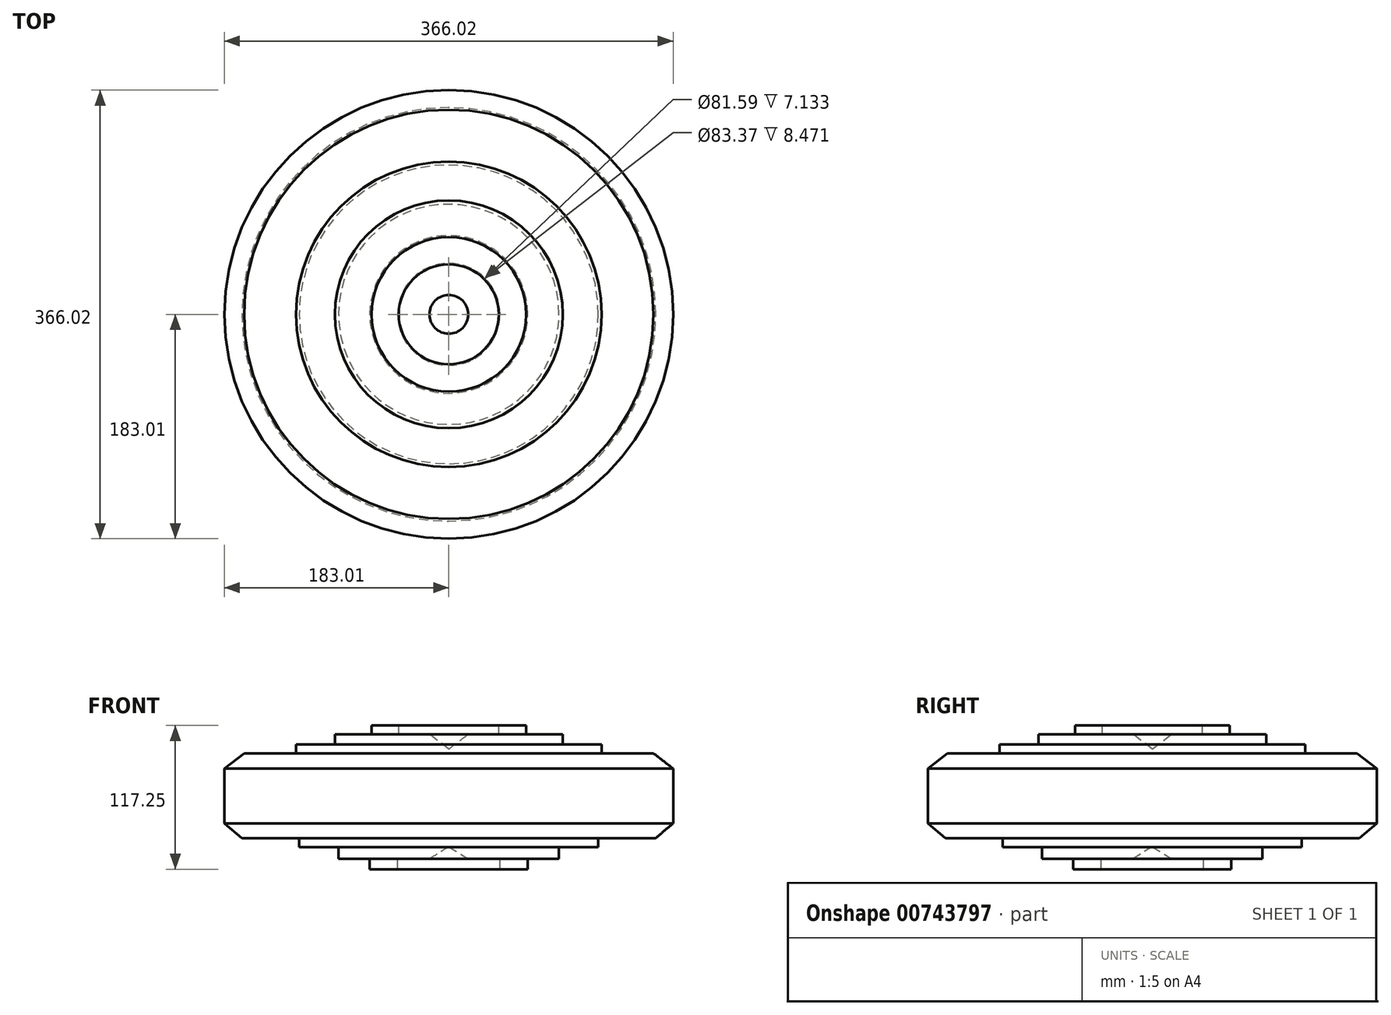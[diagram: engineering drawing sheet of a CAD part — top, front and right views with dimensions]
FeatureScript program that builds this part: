
annotation { "Feature Type Name" : "Feature", "Feature Type Description" : "" }
export const myFeature = defineFeature(function(context is Context, id is Id, definition is map)
    precondition{}
    {
        {
            var Q0;
            Q0=qCreatedBy(makeId("Front.planeOp"),FACE);
            var sketch = newSketch(context, id + "F0", { "sketchPlane" : qUnion([Q0])});
            skLineSegment(sketch, "E0", {"start": v(0, 39.9) * mm, "end": v(0, -39.9) * mm});
            skLineSegment(sketch, "E1", {"start": v(0, 39.9) * mm, "end": v(15.83, 51.94) * mm});
            skLineSegment(sketch, "E2", {"start": v(0, -39.9) * mm, "end": v(15.83, -49.7) * mm});
            skLineSegment(sketch, "E3", {"start": v(15.83, 51.94) * mm, "end": v(40.8, 51.94) * mm});
            skLineSegment(sketch, "E4", {"start": v(40.8, 51.94) * mm, "end": v(40.8, 59.07) * mm});
            skLineSegment(sketch, "E5", {"start": v(40.8, 59.07) * mm, "end": v(63.08, 59.07) * mm});
            skLineSegment(sketch, "E6", {"start": v(63.08, 59.07) * mm, "end": v(63.08, 51.94) * mm});
            skLineSegment(sketch, "E7", {"start": v(63.08, 51.94) * mm, "end": v(92.95, 51.94) * mm});
            skLineSegment(sketch, "E8", {"start": v(92.95, 51.94) * mm, "end": v(92.95, 43.47) * mm});
            skLineSegment(sketch, "E9", {"start": v(92.95, 43.47) * mm, "end": v(124.6, 43.47) * mm});
            skLineSegment(sketch, "E10", {"start": v(124.6, 43.47) * mm, "end": v(124.6, 36.33) * mm});
            skLineSegment(sketch, "E11", {"start": v(124.6, 36.33) * mm, "end": v(166.96, 36.33) * mm});
            skLineSegment(sketch, "E12", {"start": v(15.83, -49.7) * mm, "end": v(41.68, -49.7) * mm});
            skLineSegment(sketch, "E13", {"start": v(41.68, -49.7) * mm, "end": v(41.68, -58.18) * mm});
            skLineSegment(sketch, "E14", {"start": v(41.68, -58.18) * mm, "end": v(64.87, -58.18) * mm});
            skLineSegment(sketch, "E15", {"start": v(64.42, -58.63) * mm, "end": v(64.42, -49.7) * mm});
            skLineSegment(sketch, "E16", {"start": v(64.42, -49.7) * mm, "end": v(89.83, -49.7) * mm});
            skLineSegment(sketch, "E17", {"start": v(89.83, -49.7) * mm, "end": v(89.83, -40.35) * mm});
            skLineSegment(sketch, "E18", {"start": v(89.83, -40.35) * mm, "end": v(121.93, -40.35) * mm});
            skLineSegment(sketch, "E19", {"start": v(121.93, -40.35) * mm, "end": v(121.93, -32.77) * mm});
            skLineSegment(sketch, "E20", {"start": v(121.93, -32.77) * mm, "end": v(168.74, -32.77) * mm});
            skLineSegment(sketch, "E21", {"start": v(168.74, -32.77) * mm, "end": v(183, -20.73) * mm});
            skLineSegment(sketch, "E22", {"start": v(183, -20.73) * mm, "end": v(183, 23.85) * mm});
            skLineSegment(sketch, "E23", {"start": v(183, 23.85) * mm, "end": v(166.96, 36.33) * mm});
            skLineSegment(sketch, "E24", {"start": v(0, 17.16) * mm, "end": v(106.33, 17.16) * mm});
            skLineSegment(sketch, "E25", {"start": v(106.33, 17.16) * mm, "end": v(115.36, 6.46) * mm});
            skLineSegment(sketch, "E26", {"start": v(115.36, 6.46) * mm, "end": v(106.33, -7.36) * mm});
            skLineSegment(sketch, "E27", {"start": v(106.33, -7.36) * mm, "end": v(0, -7.36) * mm});
            skLineSegment(sketch, "E28", {"start": v(0, 8.7) * mm, "end": v(92.06, 8.7) * mm});
            skLineSegment(sketch, "E29", {"start": v(0, 0) * mm, "end": v(91.17, 0) * mm});
            skLineSegment(sketch, "E30", {"start": v(91.17, 0) * mm, "end": v(99.64, 5.13) * mm});
            skLineSegment(sketch, "E31", {"start": v(92.06, 8.7) * mm, "end": v(99.64, 5.13) * mm});
            skLineSegment(sketch, "E32", {"start": v(41.68, -45.7) * mm, "end": v(41.68, -7.36) * mm});
            skLineSegment(sketch, "E33", {"start": v(64.42, -49.7) * mm, "end": v(64.42, -7.36) * mm});
            skLineSegment(sketch, "E34", {"start": v(41.68, -45.7) * mm, "end": v(41.68, -49.7) * mm});
            skLineSegment(sketch, "E35", {"start": v(89.83, -40.35) * mm, "end": v(89.83, -7.36) * mm});
            skLineSegment(sketch, "E36", {"start": v(92.06, 17.16) * mm, "end": v(92.95, 43.47) * mm});
            skLineSegment(sketch, "E37", {"start": v(63.08, 51.94) * mm, "end": v(63.08, 17.16) * mm});
            skLineSegment(sketch, "E38", {"start": v(40.8, 51.94) * mm, "end": v(40.8, 17.16) * mm});
            skLineSegment(sketch, "E39", {"start": v(124.6, 36.33) * mm, "end": v(121.93, -32.77) * mm});
            skLineSegment(sketch, "E40", {"start": v(115.36, 6.46) * mm, "end": v(183, 6.46) * mm});
            skSolve(sketch);
        }
        {
            var Q0;
            {var subQ4=sQuery(id+"F0.wireOp",EDGE,"E13");Q0=makeQuery(id+"F0.imprint","IMPRINT",FACE,{"disambiguationData":[TD([[makeQuery(id+"F0.imprint","IMPRINT",EDGE,{"derivedFrom":subQ4}),1.0]])]});}
            var Q1;
            Q1=makeQuery(id+"F0.imprint","IMPRINT",FACE,{"disambiguationData":[TD([[makeQuery(id+"F0.imprint","IMPRINT",EDGE,{"derivedFrom":sQuery(id+"F0.wireOp",EDGE,"E7")}),-1.0]])]});
            var Q2;
            Q2=makeQuery(id+"F0.imprint","IMPRINT",FACE,{"disambiguationData":[TD([[makeQuery(id+"F0.imprint","IMPRINT",EDGE,{"derivedFrom":sQuery(id+"F0.wireOp",EDGE,"E9")}),-1.0]])]});
            var Q3;
            Q3=makeQuery(id+"F0.imprint","IMPRINT",FACE,{"disambiguationData":[TD([[makeQuery(id+"F0.imprint","IMPRINT",EDGE,{"derivedFrom":sQuery(id+"F0.wireOp",EDGE,"E18")}),1.0]])]});
            var Q4;
            {var subQ1=sQuery(id+"F0.wireOp",EDGE,"E20");Q4=makeQuery(id+"F0.imprint","IMPRINT",FACE,{"disambiguationData":[TD([[makeQuery(id+"F0.imprint","IMPRINT",EDGE,{"derivedFrom":subQ1}),1.0]])]});}
            var Q5;
            Q5=makeQuery(id+"F0.imprint","IMPRINT",FACE,{"disambiguationData":[TD([[makeQuery(id+"F0.imprint","IMPRINT",EDGE,{"derivedFrom":sQuery(id+"F0.wireOp",EDGE,"E16")}),1.0]])]});
            var Q6;
            {var subQ3=sQuery(id+"F0.wireOp",EDGE,"E25");Q6=makeQuery(id+"F0.imprint","IMPRINT",FACE,{"disambiguationData":[TD([[makeQuery(id+"F0.imprint","IMPRINT",EDGE,{"derivedFrom":subQ3}),-1.0]])]});}
            var Q7;
            Q7=makeQuery(id+"F0.imprint","IMPRINT",FACE,{"disambiguationData":[TD([[makeQuery(id+"F0.imprint","IMPRINT",EDGE,{"derivedFrom":sQuery(id+"F0.wireOp",EDGE,"E4")}),-1.0]])]});
            var Q8;
            {var subQ2=sQuery(id+"F0.wireOp",EDGE,"E11");Q8=makeQuery(id+"F0.imprint","IMPRINT",FACE,{"disambiguationData":[TD([[makeQuery(id+"F0.imprint","IMPRINT",EDGE,{"derivedFrom":subQ2}),-1.0]])]});}
            var Q9;
            {var subQ1=sQuery(id+"F0.wireOp",EDGE,"E28");Q9=makeQuery(id+"F0.imprint","IMPRINT",FACE,{"disambiguationData":[TD([[makeQuery(id+"F0.imprint","IMPRINT",EDGE,{"derivedFrom":subQ1}),-1.0]])]});}
            var Q10;
            {var subQ4=sQuery(id+"F0.wireOp",EDGE,"E2");Q10=makeQuery(id+"F0.imprint","IMPRINT",FACE,{"disambiguationData":[TD([[makeQuery(id+"F0.imprint","IMPRINT",EDGE,{"derivedFrom":subQ4}),1.0]])]});}
            var Q11;
            {var subQ4=sQuery(id+"F0.wireOp",EDGE,"E1");Q11=makeQuery(id+"F0.imprint","IMPRINT",FACE,{"disambiguationData":[TD([[makeQuery(id+"F0.imprint","IMPRINT",EDGE,{"derivedFrom":subQ4}),-1.0]])]});}
            var Q12;
            Q12=sQuery(id+"F0.wireOp",EDGE,"E0");
            revolve(context, id + "F1", {"surfaceOperationType" : NewSurfaceOperationType.NEW, "entities" : qUnion([Q0, Q1, Q2, Q3, Q4, Q5, Q6, Q7, Q8, Q9, Q10, Q11]), "axis" : qUnion([Q12]), "revolveType" : RevolveType.FULL});
        }
    });
